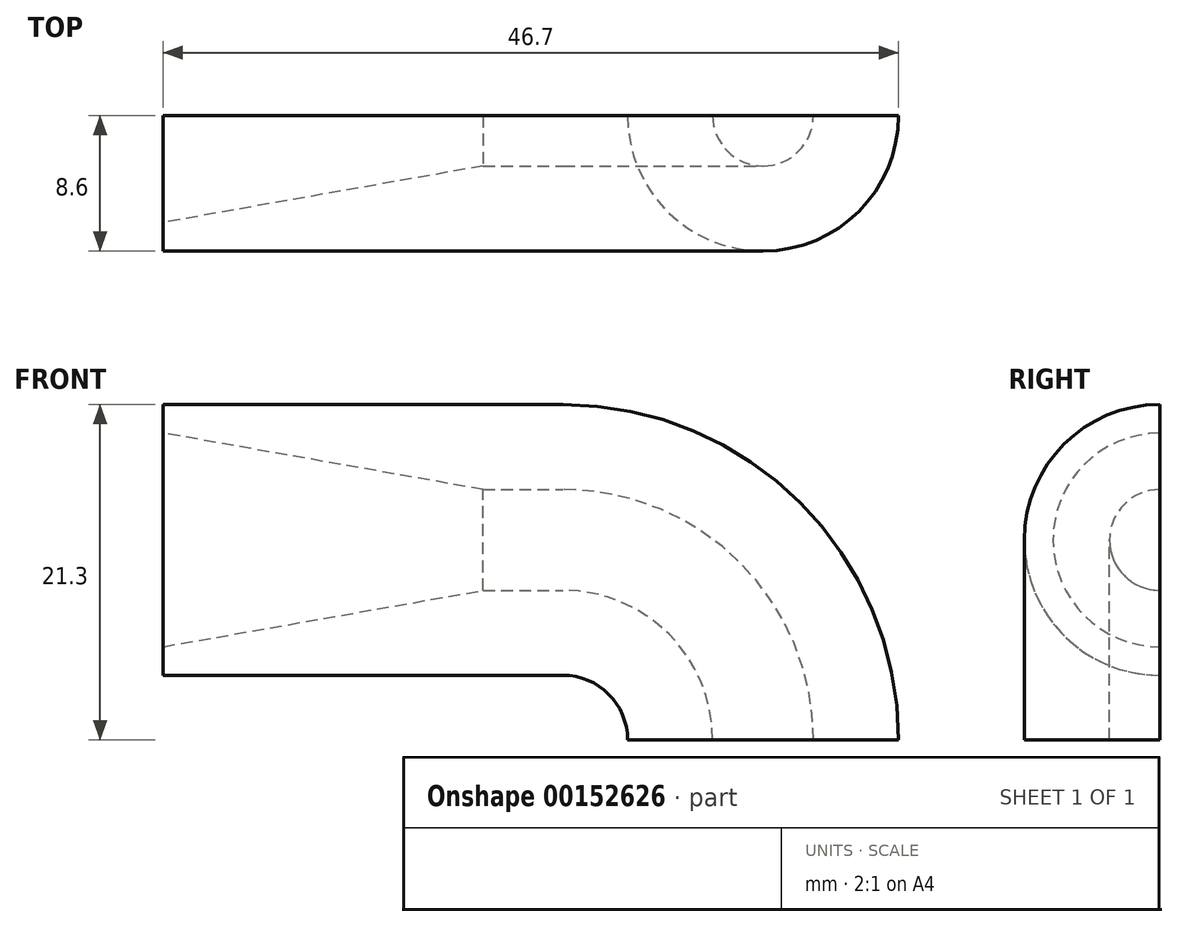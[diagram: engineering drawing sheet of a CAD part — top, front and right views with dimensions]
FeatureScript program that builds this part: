
annotation { "Feature Type Name" : "Feature", "Feature Type Description" : "" }
export const myFeature = defineFeature(function(context is Context, id is Id, definition is map)
    precondition{}
    {
        {
            var Q0;
            Q0=qCreatedBy(makeId("Top.planeOp"),FACE);
            var sketch = newSketch(context, id + "F0", { "sketchPlane" : qUnion([Q0])});
            skCircle(sketch, "E0", {"center": v(0, 0) * mm, "radius": 8.6 * mm});
            skCircle(sketch, "E1", {"center": v(0, 0) * mm, "radius": 3.2 * mm});
            skSolve(sketch);
        }
        {
            var Q0;
            Q0=qCreatedBy(makeId("Top.planeOp"),FACE);
            var sketch = newSketch(context, id + "F1", { "sketchPlane" : qUnion([Q0])});
            skLineSegment(sketch, "E2", {"start": v(-12.7, 21.46) * mm, "end": v(-12.7, -22.86) * mm});
            skSolve(sketch);
        }
        {
            var Q0;
            Q0=makeQuery(id+"F0.imprint","IMPRINT",FACE,{"disambiguationData":[TD([[makeQuery(id+"F0.imprint","IMPRINT",EDGE,{"derivedFrom":sQuery(id+"F0.wireOp",EDGE,"E0")}),1.0]])]});
            var Q1;
            Q1=sQuery(id+"F1.wireOp",EDGE,"E2");
            revolve(context, id + "F2", {"entities" : qUnion([Q0]), "axis" : qUnion([Q1]), "revolveType" : RevolveType.ONE_DIRECTION, "angle" : 90 * degree});
        }
        {
            var Q0;
            Q0=makeQuery(id+"F2.opRevolve","CAP_FACE",FACE,{"disambiguationData":[OSD([sQuery(id+"F0.wireOp",EDGE,"E0"),sQuery(id+"F0.wireOp",EDGE,"E1")])],"isStart":false});
            extrude(context, id + "F3", {"entities" : qUnion([Q0]), "operationType" : NewBodyOperationType.ADD, "depth" : 25.4 * mm});
        }
        {
            var Q0;
            Q0=makeQuery(id+"F3.opExtrude","CAP_EDGE",EDGE,{"disambiguationData":[OSD([sQuery(id+"F0.wireOp",EDGE,"E1")])],"isStart":false});
            chamfer(context, id + "F4", {"entities" : qUnion([Q0]), "chamferType" : ChamferType.OFFSET_ANGLE, "width" : 20.32 * mm, "oppositeDirection" : false, "angle" : 10 * degree, "tangentPropagation" : true});
        }
        {
            var Q0;
            Q0=qCreatedBy(makeId("Front.planeOp"),FACE);
            var sketch = newSketch(context, id + "F5", { "sketchPlane" : qUnion([Q0])});
            skLineSegment(sketch, "E3.bottom", {"start": v(-147.82, 35.46) * mm, "end": v(142.96, 35.46) * mm});
            skLineSegment(sketch, "E3.top", {"start": v(-147.82, -20.45) * mm, "end": v(142.96, -20.45) * mm});
            skLineSegment(sketch, "E3.left", {"start": v(-147.82, 35.46) * mm, "end": v(-147.82, -20.45) * mm});
            skLineSegment(sketch, "E3.right", {"start": v(142.96, 35.46) * mm, "end": v(142.96, -20.45) * mm});
            skSolve(sketch);
        }
        {
            var Q0;
            Q0 = qSketchRegion(id + "F5", true);
            extrude(context, id + "F6", {"entities" : qUnion([Q0]), "operationType" : NewBodyOperationType.REMOVE, "oppositeDirection" : true, "depth" : 25.4 * mm});
        }
    });
